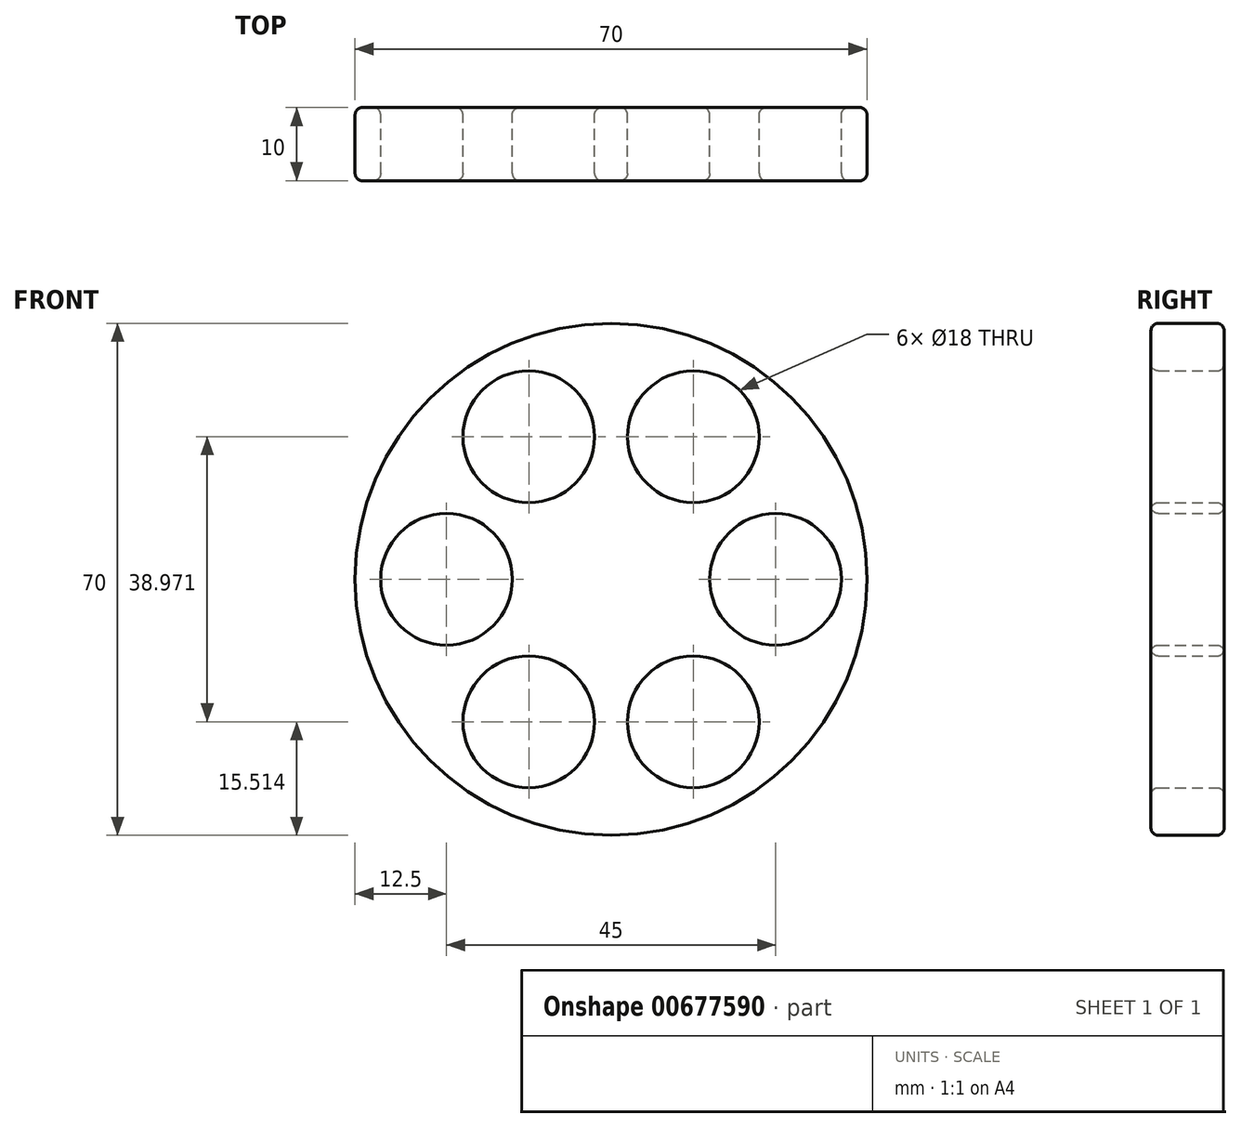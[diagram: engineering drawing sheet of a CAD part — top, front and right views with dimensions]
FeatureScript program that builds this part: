
annotation { "Feature Type Name" : "Feature", "Feature Type Description" : "" }
export const myFeature = defineFeature(function(context is Context, id is Id, definition is map)
    precondition{}
    {
        {
            var Q0;
            Q0=qCreatedBy(makeId("Front.planeOp"),FACE);
            var sketch = newSketch(context, id + "F0", { "sketchPlane" : qUnion([Q0])});
            skCircle(sketch, "E0", {"center": v(0, 0) * mm, "radius": 35 * mm});
            skCircle(sketch, "E1", {"center": v(-22.5, 0) * mm, "radius": 9 * mm});
            skCircle(sketch, "E2.1.0", {"center": v(-11.25, -19.49) * mm, "radius": 9 * mm});
            skCircle(sketch, "E2.2.0", {"center": v(11.25, -19.49) * mm, "radius": 9 * mm});
            skCircle(sketch, "E2.3.0", {"center": v(22.5, 0) * mm, "radius": 9 * mm});
            skCircle(sketch, "E2.4.0", {"center": v(11.25, 19.49) * mm, "radius": 9 * mm});
            skCircle(sketch, "E2.5.0", {"center": v(-11.25, 19.49) * mm, "radius": 9 * mm});
            skSolve(sketch);
        }
        {
            var Q0;
            Q0=makeQuery(id+"F0.imprint","IMPRINT",FACE,{"disambiguationData":[TD([[makeQuery(id+"F0.imprint","IMPRINT",EDGE,{"derivedFrom":sQuery(id+"F0.wireOp",EDGE,"E0")}),1.0]])]});
            extrude(context, id + "F1", {"entities" : qUnion([Q0]), "depth" : 5 * mm, "offsetDistance" : 25 * mm, "hasSecondDirection" : true, "secondDirectionOppositeDirection" : true, "secondDirectionDepth" : 5 * mm});
        }
        {
            var Q0;
            Q0=makeQuery(id+"F1.opExtrude","CAP_EDGE",EDGE,{"disambiguationData":[OSD([sQuery(id+"F0.wireOp",EDGE,"E0")])],"isStart":false});
            var Q1;
            Q1=makeQuery(id+"F1.opExtrude","CAP_EDGE",EDGE,{"disambiguationData":[OSD([sQuery(id+"F0.wireOp",EDGE,"E2.5.0")])],"isStart":false});
            var Q2;
            Q2=makeQuery(id+"F1.opExtrude","CAP_EDGE",EDGE,{"disambiguationData":[OSD([sQuery(id+"F0.wireOp",EDGE,"E2.4.0")])],"isStart":false});
            var Q3;
            Q3=makeQuery(id+"F1.opExtrude","CAP_EDGE",EDGE,{"disambiguationData":[OSD([sQuery(id+"F0.wireOp",EDGE,"E2.3.0")])],"isStart":false});
            var Q4;
            Q4=makeQuery(id+"F1.opExtrude","CAP_EDGE",EDGE,{"disambiguationData":[OSD([sQuery(id+"F0.wireOp",EDGE,"E2.2.0")])],"isStart":false});
            var Q5;
            Q5=makeQuery(id+"F1.opExtrude","CAP_EDGE",EDGE,{"disambiguationData":[OSD([sQuery(id+"F0.wireOp",EDGE,"E2.1.0")])],"isStart":false});
            var Q6;
            Q6=makeQuery(id+"F1.opExtrude","CAP_EDGE",EDGE,{"disambiguationData":[OSD([sQuery(id+"F0.wireOp",EDGE,"E1")])],"isStart":false});
            var Q7;
            Q7=makeQuery(id+"F1.opExtrude","CAP_EDGE",EDGE,{"disambiguationData":[OSD([sQuery(id+"F0.wireOp",EDGE,"E0")])],"isStart":true});
            var Q8;
            Q8=makeQuery(id+"F1.opExtrude","CAP_EDGE",EDGE,{"disambiguationData":[OSD([sQuery(id+"F0.wireOp",EDGE,"E2.2.0")])],"isStart":true});
            var Q9;
            Q9=makeQuery(id+"F1.opExtrude","CAP_EDGE",EDGE,{"disambiguationData":[OSD([sQuery(id+"F0.wireOp",EDGE,"E2.1.0")])],"isStart":true});
            var Q10;
            Q10=makeQuery(id+"F1.opExtrude","CAP_EDGE",EDGE,{"disambiguationData":[OSD([sQuery(id+"F0.wireOp",EDGE,"E1")])],"isStart":true});
            var Q11;
            Q11=makeQuery(id+"F1.opExtrude","CAP_EDGE",EDGE,{"disambiguationData":[OSD([sQuery(id+"F0.wireOp",EDGE,"E2.5.0")])],"isStart":true});
            var Q12;
            Q12=makeQuery(id+"F1.opExtrude","CAP_EDGE",EDGE,{"disambiguationData":[OSD([sQuery(id+"F0.wireOp",EDGE,"E2.4.0")])],"isStart":true});
            var Q13;
            Q13=makeQuery(id+"F1.opExtrude","CAP_EDGE",EDGE,{"disambiguationData":[OSD([sQuery(id+"F0.wireOp",EDGE,"E2.3.0")])],"isStart":true});
            fillet(context, id + "F2", {"entities" : qUnion([Q0, Q1, Q2, Q3, Q4, Q5, Q6, Q7, Q8, Q9, Q10, Q11, Q12, Q13]), "radius" : 1 * mm, "tangentPropagation" : true, "allowEdgeOverflow" : false});
        }
    });
